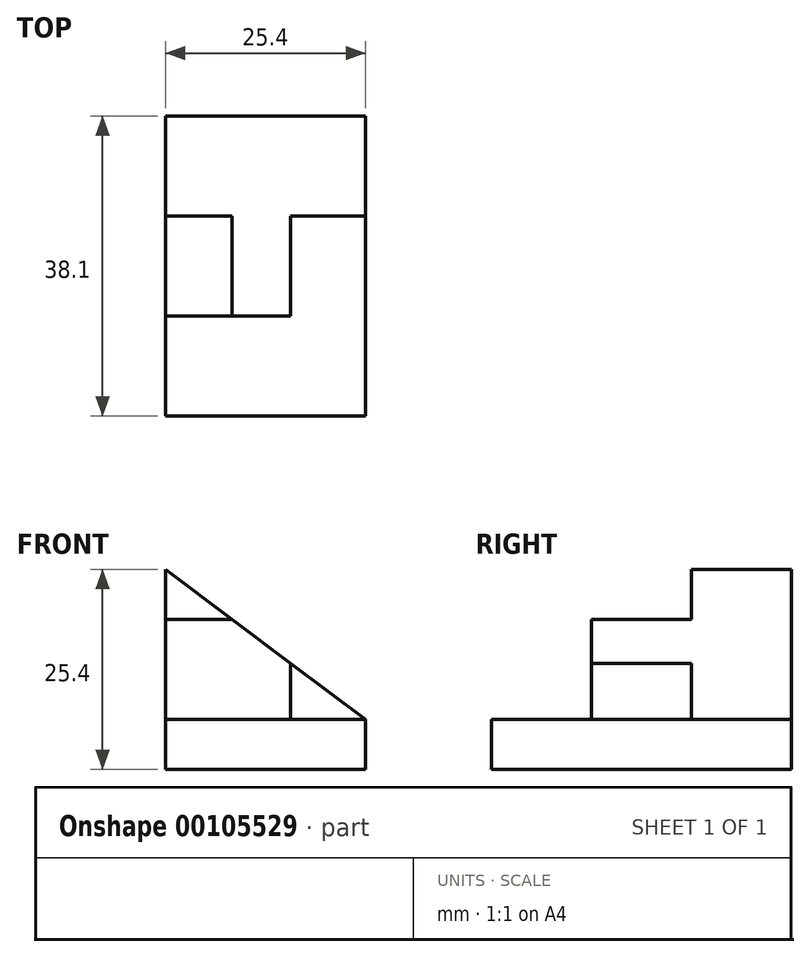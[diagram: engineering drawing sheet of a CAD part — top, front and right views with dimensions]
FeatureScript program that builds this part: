
annotation { "Feature Type Name" : "Feature", "Feature Type Description" : "" }
export const myFeature = defineFeature(function(context is Context, id is Id, definition is map)
    precondition{}
    {
        {
            var Q0;
            Q0=qCreatedBy(makeId("Right.planeOp"),FACE);
            var sketch = newSketch(context, id + "F0", { "sketchPlane" : qUnion([Q0])});
            skLineSegment(sketch, "E0", {"start": v(0, 0) * mm, "end": v(0, 6.35) * mm});
            skLineSegment(sketch, "E1", {"start": v(0, 6.35) * mm, "end": v(-38.1, 6.35) * mm});
            skLineSegment(sketch, "E2", {"start": v(-38.1, 6.35) * mm, "end": v(-38.1, 0) * mm});
            skLineSegment(sketch, "E3", {"start": v(-38.1, 0) * mm, "end": v(0, 0) * mm});
            skSolve(sketch);
        }
        {
            var Q0;
            Q0=makeQuery(id+"F0.imprint","IMPRINT",FACE,{"disambiguationData":[TD([[makeQuery(id+"F0.imprint","IMPRINT",EDGE,{"derivedFrom":sQuery(id+"F0.wireOp",EDGE,"E0")}),1.0]])]});
            extrude(context, id + "F1", {"entities" : qUnion([Q0]), "depth" : 25.4 * mm});
        }
        {
            var Q0;
            Q0=qCreatedBy(makeId("Right.planeOp"),FACE);
            var sketch = newSketch(context, id + "F2", { "sketchPlane" : qUnion([Q0])});
            skLineSegment(sketch, "E4", {"start": v(0, 0) * mm, "end": v(0, 5.42) * mm});
            skLineSegment(sketch, "E5", {"start": v(0, 0) * mm, "end": v(0, 25.4) * mm});
            skLineSegment(sketch, "E6", {"start": v(0, 25.4) * mm, "end": v(-12.7, 25.4) * mm});
            skLineSegment(sketch, "E7", {"start": v(-12.7, 25.4) * mm, "end": v(-12.7, 19.05) * mm});
            skLineSegment(sketch, "E8", {"start": v(-12.7, 19.05) * mm, "end": v(-12.7, 0) * mm});
            skLineSegment(sketch, "E9", {"start": v(-12.7, 0) * mm, "end": v(0, 0) * mm});
            skSolve(sketch);
        }
        {
            var Q0;
            {var subQ0=sQuery(id+"F2.wireOp",EDGE,"E6");Q0=makeQuery(id+"F2.imprint","IMPRINT",FACE,{"disambiguationData":[TD([[makeQuery(id+"F2.imprint","IMPRINT",EDGE,{"derivedFrom":subQ0}),1.0]])]});}
            extrude(context, id + "F3", {"entities" : qUnion([Q0]), "operationType" : NewBodyOperationType.ADD, "depth" : 25.4 * mm});
        }
        {
            var Q0;
            Q0=qCreatedBy(makeId("Right.planeOp"),FACE);
            var sketch = newSketch(context, id + "F4", { "sketchPlane" : qUnion([Q0])});
            skLineSegment(sketch, "E10", {"start": v(-12.7, 6.35) * mm, "end": v(-12.7, 19.05) * mm});
            skLineSegment(sketch, "E11", {"start": v(-12.7, 19.05) * mm, "end": v(-25.4, 19.05) * mm});
            skLineSegment(sketch, "E12", {"start": v(-25.4, 19.05) * mm, "end": v(-25.4, 6.35) * mm});
            skLineSegment(sketch, "E13", {"start": v(-25.4, 6.35) * mm, "end": v(-12.7, 6.35) * mm});
            skLineSegment(sketch, "E14", {"start": v(0, 0) * mm, "end": v(0, 6.35) * mm, "construction": true});
            skLineSegment(sketch, "E15", {"start": v(0, 6.35) * mm, "end": v(-12.7, 6.35) * mm, "construction": true});
            skSolve(sketch);
        }
        {
            var Q0;
            Q0=qCreatedBy(makeId("Front.planeOp"),FACE);
            var sketch = newSketch(context, id + "F5", { "sketchPlane" : qUnion([Q0])});
            skLineSegment(sketch, "E16", {"start": v(0, 0) * mm, "end": v(0, 25.4) * mm});
            skLineSegment(sketch, "E17", {"start": v(0, 0) * mm, "end": v(25.4, 0) * mm});
            skLineSegment(sketch, "E18", {"start": v(25.4, 0) * mm, "end": v(25.4, 6.35) * mm});
            skLineSegment(sketch, "E19", {"start": v(25.4, 6.35) * mm, "end": v(0, 25.4) * mm});
            skSolve(sketch);
        }
        {
            var Q0;
            Q0=makeQuery(id+"F4.imprint","IMPRINT",FACE,{"disambiguationData":[TD([[makeQuery(id+"F4.imprint","IMPRINT",EDGE,{"derivedFrom":sQuery(id+"F4.wireOp",EDGE,"E10")}),1.0]])]});
            extrude(context, id + "F6", {"entities" : qUnion([Q0]), "operationType" : NewBodyOperationType.ADD, "depth" : 15.88 * mm});
        }
        {
            var Q0;
            Q0 = qSketchRegion(id + "F5", true);
            extrude(context, id + "F7", {"entities" : qUnion([Q0]), "operationType" : NewBodyOperationType.INTERSECT, "depth" : 38.1 * mm});
        }
    });
